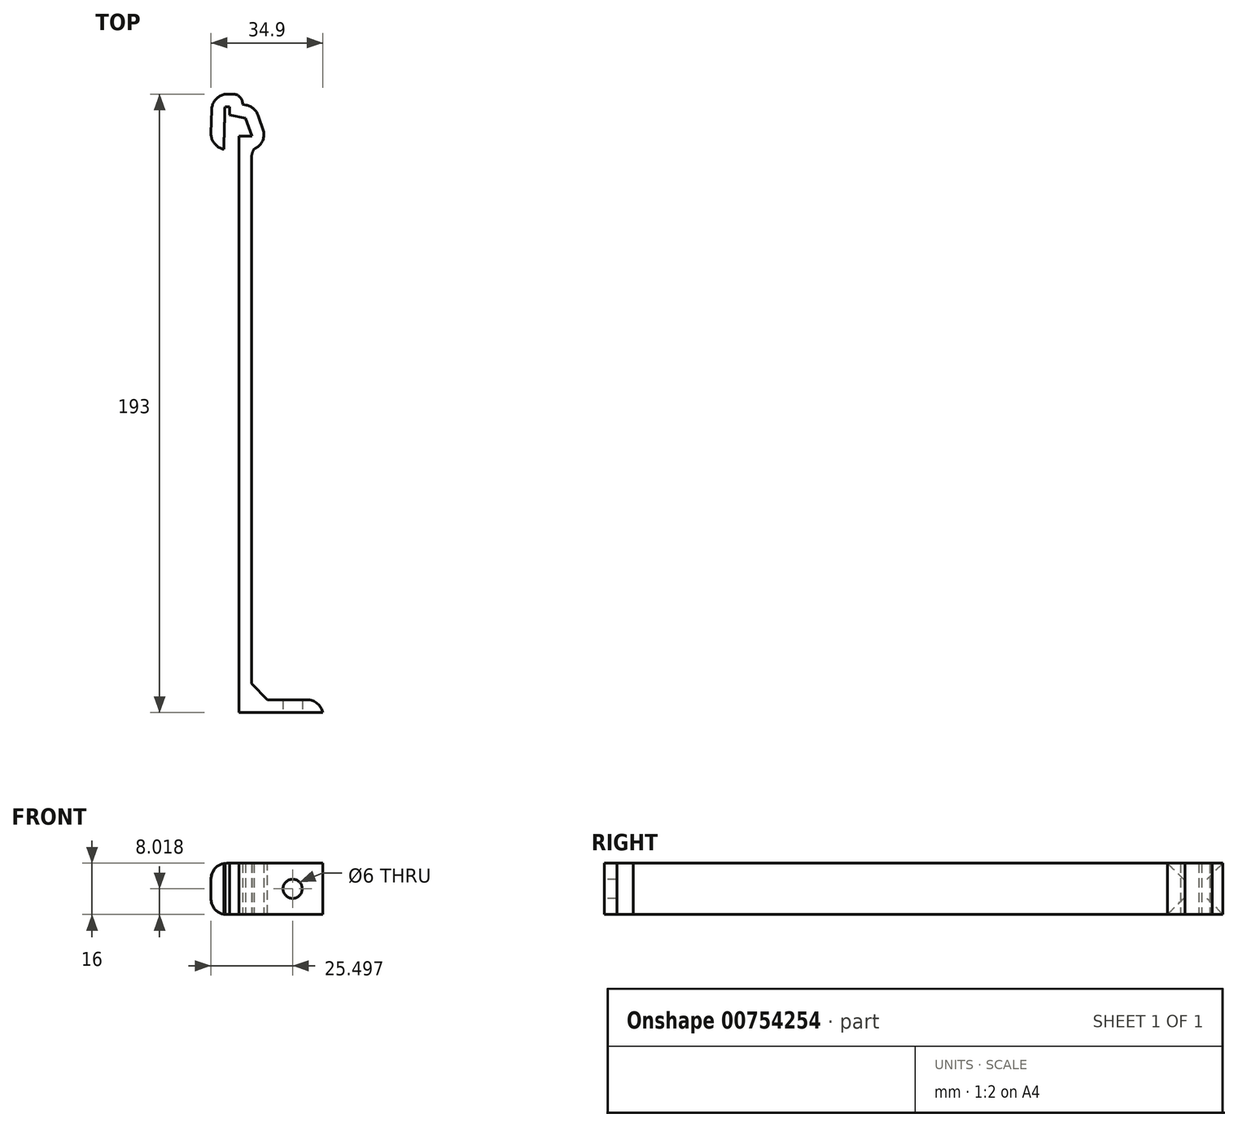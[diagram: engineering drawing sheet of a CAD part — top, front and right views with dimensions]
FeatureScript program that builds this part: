
annotation { "Feature Type Name" : "Feature", "Feature Type Description" : "" }
export const myFeature = defineFeature(function(context is Context, id is Id, definition is map)
    precondition{}
    {
        {
            var Q0;
            Q0=qCreatedBy(makeId("Top.planeOp"),FACE);
            var sketch = newSketch(context, id + "F0", { "sketchPlane" : qUnion([Q0])});
            skLineSegment(sketch, "E0", {"start": v(1.5, 0) * mm, "end": v(1.5, 2.5) * mm});
            skLineSegment(sketch, "E1", {"start": v(1.5, 2.5) * mm, "end": v(0, 2.5) * mm});
            skPoint(sketch, "E2", {"position": v(6.4, -1) * mm});
            skLineSegment(sketch, "E3", {"start": v(1.5, 0) * mm, "end": v(6.4, -1) * mm});
            skLineSegment(sketch, "E4", {"start": v(8.4, -7.43) * mm, "end": v(8.4, -1) * mm, "construction": true});
            skLineSegment(sketch, "E5", {"start": v(6.4, -1) * mm, "end": v(8.4, -6.66) * mm});
            skLineSegment(sketch, "E6.0", {"start": v(9.42, 2.47) * mm, "end": v(12.17, -5.32) * mm});
            skLineSegment(sketch, "E6.2", {"start": v(5.5, 6.5) * mm, "end": v(-4.03, 6.5) * mm});
            skLineSegment(sketch, "E6.3", {"start": v(5.5, 3.27) * mm, "end": v(5.5, 6.5) * mm});
            skLineSegment(sketch, "E6.4", {"start": v(5.5, 3.27) * mm, "end": v(9.42, 2.47) * mm});
            skLineSegment(sketch, "E7", {"start": v(1.5, 0) * mm, "end": v(1.5, -9.75) * mm, "construction": true});
            skLineSegment(sketch, "E8", {"start": v(8.4, -6.66) * mm, "end": v(4.31, -6.66) * mm});
            skLineSegment(sketch, "E9.0", {"start": v(9.09, -10.66) * mm, "end": v(8.31, -10.66) * mm});
            skLineSegment(sketch, "E9.1", {"start": v(9.09, -10.66) * mm, "end": v(12.17, -9.57) * mm});
            skLineSegment(sketch, "E10", {"start": v(12.17, -5.32) * mm, "end": v(12.17, -9.57) * mm});
            skLineSegment(sketch, "E11", {"start": v(0, 27.06) * mm, "end": v(0, -19.04) * mm, "construction": true});
            skLineSegment(sketch, "E12", {"start": v(-104, 32.98) * mm, "end": v(-104, -15.05) * mm, "construction": true});
            skLineSegment(sketch, "E13", {"start": v(-104, -15.05) * mm, "end": v(-104, -177.8) * mm, "construction": true});
            skLineSegment(sketch, "E14", {"start": v(-4.5, -10.6) * mm, "end": v(-4.03, 6.5) * mm});
            skLineSegment(sketch, "E15", {"start": v(-0.38, -10.72) * mm, "end": v(0, 2.5) * mm});
            skLineSegment(sketch, "E16.right", {"start": v(4.31, -10.66) * mm, "end": v(4.31, -14.66) * mm});
            skLineSegment(sketch, "E17", {"start": v(4.31, -14.66) * mm, "end": v(4.31, -186.5) * mm});
            skLineSegment(sketch, "E18", {"start": v(5.5, 6.5) * mm, "end": v(56.75, 6.5) * mm, "construction": true});
            skLineSegment(sketch, "E19", {"start": v(56.75, 6.5) * mm, "end": v(56.75, -186.5) * mm, "construction": true});
            skLineSegment(sketch, "E20", {"start": v(56.75, -186.5) * mm, "end": v(4.31, -186.5) * mm, "construction": true});
            skPoint(sketch, "E21", {"position": v(8.31, -10.66) * mm});
            skLineSegment(sketch, "E22", {"start": v(4.31, -186.5) * mm, "end": v(8.31, -186.5) * mm});
            skLineSegment(sketch, "E23", {"start": v(8.31, -182.5) * mm, "end": v(8.31, -10.66) * mm});
            skLineSegment(sketch, "E24", {"start": v(-0.38, -10.72) * mm, "end": v(-4.5, -10.6) * mm});
            skLineSegment(sketch, "E25", {"start": v(8.31, -186.5) * mm, "end": v(30.53, -186.5) * mm});
            skLineSegment(sketch, "E26", {"start": v(30.53, -186.5) * mm, "end": v(30.53, -182.5) * mm});
            skLineSegment(sketch, "E27", {"start": v(30.53, -182.5) * mm, "end": v(8.31, -182.5) * mm});
            skLineSegment(sketch, "E28", {"start": v(4.31, -10.66) * mm, "end": v(4.31, -6.66) * mm});
            skSolve(sketch);
        }
        {
            var Q0;
            Q0=makeQuery(id+"F0.imprint","IMPRINT",FACE,{"disambiguationData":[TD([[makeQuery(id+"F0.imprint","IMPRINT",EDGE,{"derivedFrom":sQuery(id+"F0.wireOp",EDGE,"E0")}),-1.0]])]});
            extrude(context, id + "F1", {"entities" : qUnion([Q0]), "depth" : 16 * mm, "offsetDistance" : 25 * mm});
        }
        {
            var Q0;
            Q0=makeQuery(id+"F1.opExtrude","SWEPT_FACE",FACE,{"disambiguationData":[OSD([sQuery(id+"F0.wireOp",EDGE,"E22"),sQuery(id+"F0.wireOp",EDGE,"E25")])]});
            var sketch = newSketch(context, id + "F2", { "sketchPlane" : qUnion([Q0])});
            skLineSegment(sketch, "E29", {"start": v(4.31, 0) * mm, "end": v(30.53, 16) * mm, "construction": true});
            skLineSegment(sketch, "E30", {"start": v(30.53, 16) * mm, "end": v(30.53, 0) * mm, "construction": true});
            skLineSegment(sketch, "E31", {"start": v(30.53, 0) * mm, "end": v(4.31, 16) * mm, "construction": true});
            skCircle(sketch, "E32", {"center": v(21.13, 8.02) * mm, "radius": 3 * mm});
            skLineSegment(sketch, "E33", {"start": v(17.42, 8) * mm, "end": v(30.53, 8) * mm, "construction": true});
            skSolve(sketch);
        }
        {
            var Q0;
            Q0 = qSketchRegion(id + "F2", true);
            extrude(context, id + "F3", {"entities" : qUnion([Q0]), "operationType" : NewBodyOperationType.REMOVE, "oppositeDirection" : true, "depth" : 25 * mm, "offsetDistance" : 25 * mm});
        }
        {
            var Q0;
            Q0=makeQuery(id+"F1.opExtrude","SWEPT_EDGE",EDGE,{"disambiguationData":[OSD([sQuery(id+"F0.wireOp",EDGE,"E23"),sQuery(id+"F0.wireOp",EDGE,"E27")])]});
            chamfer(context, id + "F4", {"entities" : qUnion([Q0]), "width" : 5 * mm, "tangentPropagation" : true});
        }
        {
            var Q0;
            Q0=makeQuery(id+"F1.opExtrude","SWEPT_EDGE",EDGE,{"disambiguationData":[OSD([sQuery(id+"F0.wireOp",EDGE,"E26"),sQuery(id+"F0.wireOp",EDGE,"E27")])]});
            var Q1;
            Q1=makeQuery(id+"F1.opExtrude","SWEPT_EDGE",EDGE,{"disambiguationData":[OSD([sQuery(id+"F0.wireOp",EDGE,"E6.2"),sQuery(id+"F0.wireOp",EDGE,"E14")])]});
            var Q2;
            Q2=makeQuery(id+"F1.opExtrude","SWEPT_EDGE",EDGE,{"disambiguationData":[OSD([sQuery(id+"F0.wireOp",EDGE,"E9.0"),sQuery(id+"F0.wireOp",EDGE,"E23")])]});
            var Q3;
            Q3=makeQuery(id+"F1.opExtrude","SWEPT_EDGE",EDGE,{"disambiguationData":[OSD([sQuery(id+"F0.wireOp",EDGE,"E9.1"),sQuery(id+"F0.wireOp",EDGE,"E10")])]});
            var Q4;
            Q4=makeQuery(id+"F1.opExtrude","SWEPT_EDGE",EDGE,{"disambiguationData":[OSD([sQuery(id+"F0.wireOp",EDGE,"E6.0"),sQuery(id+"F0.wireOp",EDGE,"E6.4")])]});
            var Q5;
            Q5=makeQuery(id+"F1.opExtrude","SWEPT_FACE",FACE,{"disambiguationData":[OSD([sQuery(id+"F0.wireOp",EDGE,"E14")])]});
            fillet(context, id + "F5", {"entities" : qUnion([Q0, Q1, Q2, Q3, Q4, Q5]), "radius" : 5 * mm, "tangentPropagation" : true, "allowEdgeOverflow" : false});
        }
        {
            var Q0;
            Q0=makeQuery(id+"F1.opExtrude","SWEPT_EDGE",EDGE,{"disambiguationData":[OSD([sQuery(id+"F0.wireOp",EDGE,"E6.2"),sQuery(id+"F0.wireOp",EDGE,"E6.3")])]});
            fillet(context, id + "F6", {"entities" : qUnion([Q0]), "radius" : 3 * mm, "tangentPropagation" : true, "allowEdgeOverflow" : false});
        }
    });
